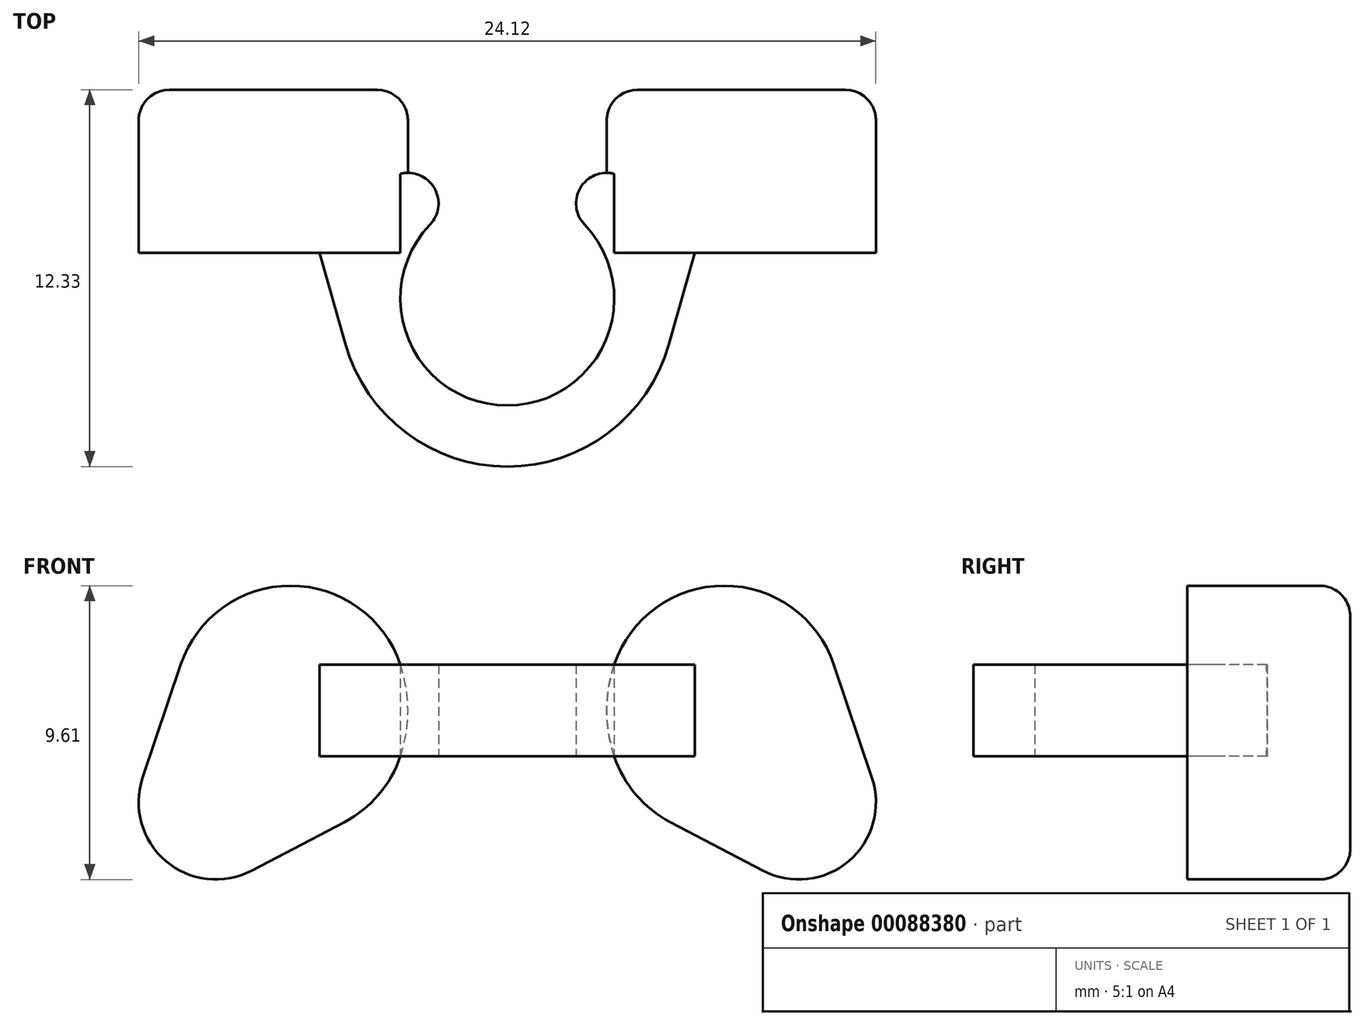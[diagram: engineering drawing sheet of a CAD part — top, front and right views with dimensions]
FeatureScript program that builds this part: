
annotation { "Feature Type Name" : "Feature", "Feature Type Description" : "" }
export const myFeature = defineFeature(function(context is Context, id is Id, definition is map)
    precondition{}
    {
        {
            var Q0;
            Q0=qCreatedBy(makeId("Top.planeOp"),FACE);
            var sketch = newSketch(context, id + "F0", { "sketchPlane" : qUnion([Q0])});
            skLineSegment(sketch, "E0", {"start": v(-2.53, 0) * mm, "end": v(2.53, 0) * mm, "construction": true});
            skArc(sketch, "E1", {"start": v(-2.53, 0) * mm, "mid": v(0, -5.92) * mm, "end": v(2.53, 0) * mm});
            skLineSegment(sketch, "E2", {"start": v(0, -2.42) * mm, "end": v(2.53, 0) * mm, "construction": true});
            skLineSegment(sketch, "E3", {"start": v(2.53, 0) * mm, "end": v(3.97, 1.38) * mm, "construction": true});
            skLineSegment(sketch, "E4", {"start": v(0, -2.42) * mm, "end": v(-2.53, 0) * mm, "construction": true});
            skLineSegment(sketch, "E5", {"start": v(-2.53, 0) * mm, "end": v(-3.97, 1.38) * mm, "construction": true});
            skArc(sketch, "E6", {"start": v(-2.53, 0) * mm, "mid": v(-2.56, 1.41) * mm, "end": v(-3.97, 1.38) * mm});
            skArc(sketch, "E7", {"start": v(3.97, 1.38) * mm, "mid": v(2.56, 1.41) * mm, "end": v(2.53, 0) * mm});
            skArc(sketch, "E8", {"start": v(-3.97, 1.38) * mm, "mid": v(0, -7.92) * mm, "end": v(3.97, 1.38) * mm});
            skArc(sketch, "E9", {"start": v(3.97, 1.38) * mm, "mid": v(0, 3.08) * mm, "end": v(-3.97, 1.38) * mm, "construction": true});
            skLineSegment(sketch, "E10", {"start": v(0, -2.42) * mm, "end": v(11, -2.42) * mm, "construction": true});
            skLineSegment(sketch, "E11", {"start": v(0, -2.42) * mm, "end": v(-11, -2.42) * mm, "construction": true});
            skLineSegment(sketch, "E12.bottom", {"start": v(-11, -2.42) * mm, "end": v(-5.5, -2.42) * mm});
            skLineSegment(sketch, "E12.top", {"start": v(-11, -7.92) * mm, "end": v(-5.5, -7.92) * mm});
            skLineSegment(sketch, "E12.left", {"start": v(-11, -2.42) * mm, "end": v(-11, -7.92) * mm});
            skLineSegment(sketch, "E12.right", {"start": v(-5.5, -2.42) * mm, "end": v(-5.5, -7.92) * mm});
            skLineSegment(sketch, "E13.bottom", {"start": v(11, -2.42) * mm, "end": v(5.5, -2.42) * mm});
            skLineSegment(sketch, "E13.top", {"start": v(11, -7.92) * mm, "end": v(5.5, -7.92) * mm});
            skLineSegment(sketch, "E13.left", {"start": v(11, -2.42) * mm, "end": v(11, -7.92) * mm});
            skLineSegment(sketch, "E13.right", {"start": v(5.5, -2.42) * mm, "end": v(5.5, -7.92) * mm});
            skLineSegment(sketch, "E14", {"start": v(-10.9, -2.42) * mm, "end": v(-10.9, -7.92) * mm});
            skLineSegment(sketch, "E15", {"start": v(10.9, -2.42) * mm, "end": v(10.9, -7.92) * mm});
            skSolve(sketch);
        }
        {
            var Q0;
            {var subQ0=sQuery(id+"F0.wireOp",EDGE,"E12.right");Q0=makeQuery(id+"F0.imprint","IMPRINT",FACE,{"disambiguationData":[TD([[makeQuery(id+"F0.imprint","IMPRINT",EDGE,{"derivedFrom":subQ0}),-1.0]])]});}
            var Q1;
            Q1=sQuery(id+"F0.wireOp",EDGE,"E12.right");
            revolve(context, id + "F1", {"entities" : qUnion([Q0]), "axis" : qUnion([Q1]), "revolveType" : RevolveType.FULL});
        }
        {
            var Q0;
            Q0=makeQuery(id+"F0.imprint","IMPRINT",FACE,{"disambiguationData":[TD([[makeQuery(id+"F0.imprint","IMPRINT",EDGE,{"derivedFrom":sQuery(id+"F0.wireOp",EDGE,"E1")}),-1.0]])]});
            extrude(context, id + "F2", {"entities" : qUnion([Q0]), "operationType" : NewBodyOperationType.ADD, "endBound" : BoundingType.SYMMETRIC, "depth" : 3 * mm});
        }
        {
            var Q0;
            {var subQ0=sQuery(id+"F0.wireOp",EDGE,"E13.right");Q0=makeQuery(id+"F0.imprint","IMPRINT",FACE,{"disambiguationData":[TD([[makeQuery(id+"F0.imprint","IMPRINT",EDGE,{"derivedFrom":subQ0}),1.0]])]});}
            var Q1;
            Q1=sQuery(id+"F0.wireOp",EDGE,"E13.right");
            revolve(context, id + "F3", {"operationType" : NewBodyOperationType.ADD, "entities" : qUnion([Q0]), "axis" : qUnion([Q1]), "revolveType" : RevolveType.FULL});
        }
        {
            var Q0;
            Q0=qCreatedBy(makeId("Top.planeOp"),FACE);
            var sketch = newSketch(context, id + "F4", { "sketchPlane" : qUnion([Q0])});
            skArc(sketch, "E16.0", {"start": v(-2.53, 0) * mm, "mid": v(0, -5.92) * mm, "end": v(2.53, 0) * mm});
            skLineSegment(sketch, "E17", {"start": v(-2.53, 0) * mm, "end": v(2.53, 0) * mm});
            skSolve(sketch);
        }
        {
            var Q0;
            Q0 = qSketchRegion(id + "F4", true);
            extrude(context, id + "F5", {"entities" : qUnion([Q0]), "operationType" : NewBodyOperationType.REMOVE, "endBound" : BoundingType.SYMMETRIC, "oppositeDirection" : true, "depth" : 25 * mm});
        }
        {
            var Q0;
            Q0=makeQuery(id+"F1.opRevolve","SWEPT_FACE",FACE,{"disambiguationData":[OSD([sQuery(id+"F0.wireOp",EDGE,"E12.bottom")])]});
            var sketch = newSketch(context, id + "F6", { "sketchPlane" : qUnion([Q0])});
            skLineSegment(sketch, "E18.0", {"start": v(3.5, 5.02) * mm, "end": v(3.5, 1.5) * mm});
            skLineSegment(sketch, "E19.0", {"start": v(-3.5, 1.5) * mm, "end": v(-3.5, 5.02) * mm});
            skLineSegment(sketch, "E20", {"start": v(-3.5, 1.5) * mm, "end": v(3.5, 1.5) * mm});
            skLineSegment(sketch, "E21", {"start": v(3.5, 5.02) * mm, "end": v(-3.5, 5.02) * mm});
            skLineSegment(sketch, "E22.0", {"start": v(-3.5, -5.02) * mm, "end": v(-3.5, -1.5) * mm});
            skLineSegment(sketch, "E23.0", {"start": v(3.5, -1.5) * mm, "end": v(3.5, -5.02) * mm});
            skLineSegment(sketch, "E24", {"start": v(3.5, -1.5) * mm, "end": v(-3.5, -1.5) * mm});
            skLineSegment(sketch, "E25", {"start": v(-3.5, -5.02) * mm, "end": v(3.5, -5.02) * mm});
            skSolve(sketch);
        }
        {
            var Q0;
            Q0 = qSketchRegion(id + "F6", true);
            extrude(context, id + "F7", {"entities" : qUnion([Q0]), "operationType" : NewBodyOperationType.REMOVE, "oppositeDirection" : true, "depth" : 25 * mm});
        }
        {
            var Q0;
            Q0=makeQuery(id+"F3.opRevolve","SWEPT_FACE",FACE,{"disambiguationData":[OSD([sQuery(id+"F0.wireOp",EDGE,"E13.top")])]});
            var sketch = newSketch(context, id + "F8", { "sketchPlane" : qUnion([Q0])});
            skArc(sketch, "E26", {"start": v(3.5, -1.5) * mm, "mid": v(7.1, -4.08) * mm, "end": v(10.69, -1.5) * mm});
            skArc(sketch, "E27", {"start": v(10.69, 1.5) * mm, "mid": v(7.1, 4.08) * mm, "end": v(3.5, 1.5) * mm});
            skSolve(sketch);
        }
        {
            var Q0;
            Q0 = qSketchRegion(id + "F8", true);
            var Q1;
            {var subQ0=sQuery(id+"F8.wireOp",EDGE,"E26");Q1=makeQuery(id+"F8.imprint","IMPRINT",FACE,{"disambiguationData":[TD([[makeQuery(id+"F8.imprint","IMPRINT",EDGE,{"derivedFrom":subQ0}),-1.0]])]});}
            var Q2;
            {var subQ0=sQuery(id+"F8.wireOp",EDGE,"E27");Q2=makeQuery(id+"F8.imprint","IMPRINT",FACE,{"disambiguationData":[TD([[makeQuery(id+"F8.imprint","IMPRINT",EDGE,{"derivedFrom":subQ0}),-1.0]])]});}
            extrude(context, id + "F9", {"entities" : qUnion([Q0, Q1, Q2]), "operationType" : NewBodyOperationType.REMOVE, "oppositeDirection" : true, "depth" : 25 * mm});
        }
        {
            var Q0;
            Q0=makeQuery(id+"F3.opRevolve","SWEPT_FACE",FACE,{"disambiguationData":[OSD([sQuery(id+"F0.wireOp",EDGE,"E13.top")])]});
            var sketch = newSketch(context, id + "F10", { "sketchPlane" : qUnion([Q0])});
            skLineSegment(sketch, "E28.0", {"start": v(-0.31, -1.5) * mm, "end": v(0.31, -1.5) * mm});
            skLineSegment(sketch, "E29.0", {"start": v(-0.31, 1.5) * mm, "end": v(0.31, 1.5) * mm});
            skLineSegment(sketch, "E30", {"start": v(0, -1.5) * mm, "end": v(0, 1.5) * mm});
            skLineSegment(sketch, "E31", {"start": v(-0.31, -1.5) * mm, "end": v(-0.31, 1.5) * mm});
            skSolve(sketch);
        }
        {
            var Q0;
            {var subQ2=sQuery(id+"F10.wireOp",EDGE,"E30");Q0=makeQuery(id+"F10.imprint","IMPRINT",FACE,{"disambiguationData":[TD([[makeQuery(id+"F10.imprint","IMPRINT",EDGE,{"derivedFrom":subQ2}),1.0]])]});}
            var Q1;
            Q1=makeQuery(id+"F1.opRevolve","SWEPT_FACE",FACE,{"disambiguationData":[OSD([sQuery(id+"F0.wireOp",EDGE,"E12.top")])]});
            extrude(context, id + "F11", {"entities" : qUnion([Q0, Q1]), "operationType" : NewBodyOperationType.REMOVE, "oppositeDirection" : true, "depth" : 25 * mm});
        }
        {
            var Q0;
            Q0=makeQuery(id+"F3.opRevolve","SWEPT_FACE",FACE,{"disambiguationData":[OSD([sQuery(id+"F0.wireOp",EDGE,"E13.top")])]});
            var sketch = newSketch(context, id + "F12", { "sketchPlane" : qUnion([Q0])});
            skArc(sketch, "E32.0.0", {"start": v(10.69, -1.5) * mm, "mid": v(10.9, 0) * mm, "end": v(10.69, 1.5) * mm});
            skArc(sketch, "E32.0.1", {"start": v(10.69, 1.5) * mm, "mid": v(7.1, 4.08) * mm, "end": v(3.5, 1.5) * mm});
            skLineSegment(sketch, "E32.0.2", {"start": v(3.5, 1.5) * mm, "end": v(0.31, 1.5) * mm});
            skArc(sketch, "E32.0.3", {"start": v(0.31, 1.5) * mm, "mid": v(0.1, 0) * mm, "end": v(0.31, -1.5) * mm});
            skLineSegment(sketch, "E32.0.4", {"start": v(0.31, -1.5) * mm, "end": v(3.5, -1.5) * mm});
            skArc(sketch, "E32.0.5", {"start": v(3.5, -1.5) * mm, "mid": v(7.1, -4.08) * mm, "end": v(10.69, -1.5) * mm});
            skArc(sketch, "E33", {"start": v(3.5, 1.5) * mm, "mid": v(3.25, 0) * mm, "end": v(3.5, -1.5) * mm});
            skSolve(sketch);
        }
        {
            var Q0;
            Q0=makeQuery(id+"F12.imprint","IMPRINT",FACE,{"disambiguationData":[TD([[makeQuery(id+"F12.imprint","IMPRINT",EDGE,{"derivedFrom":sQuery(id+"F12.wireOp",EDGE,"E32.0.0")}),-1.0]])]});
            extrude(context, id + "F13", {"entities" : qUnion([Q0]), "operationType" : NewBodyOperationType.ADD, "oppositeDirection" : true, "depth" : 9.33 * mm});
        }
        {
            var Q0;
            {var subQ0=sQuery(id+"F0.wireOp",EDGE,"E1");var subQ2=sQuery(id+"F0.wireOp",EDGE,"E7");var subQ3=makeQuery(id+"F2.opExtrude","SWEPT_FACE",FACE,{"disambiguationData":[OSD([subQ2])]});var subQ4=sQuery(id+"F0.wireOp",EDGE,"E8");Q0=makeQuery(id+"F3.boolean.opBoolean","SPLIT",FACE,{"disambiguationData":[TD([subQ3])],"derivedFrom":makeQuery(id+"F2.boolean.opBoolean","SPLIT",FACE,{"disambiguationData":[TD([makeQuery(id+"F1.opRevolve","SWEPT_FACE",FACE,{"disambiguationData":[OSD([sQuery(id+"F0.wireOp",EDGE,"E14")])]})])],"derivedFrom":makeQuery(id+"F2.opExtrude","CAP_FACE",FACE,{"disambiguationData":[OSD([subQ0,sQuery(id+"F0.wireOp",EDGE,"E6"),subQ2,subQ4])],"isStart":false})})});}
            var sketch = newSketch(context, id + "F14", { "sketchPlane" : qUnion([Q0])});
            skArc(sketch, "E34.0", {"start": v(0, -5.92) * mm, "mid": v(2.47, -4.9) * mm, "end": v(3.5, -2.42) * mm});
            skArc(sketch, "E35.0", {"start": v(3.5, -2.42) * mm, "mid": v(3.25, -1.12) * mm, "end": v(2.53, 0) * mm});
            skLineSegment(sketch, "E36", {"start": v(2.53, 0) * mm, "end": v(0, -5.92) * mm});
            skArc(sketch, "E37.0", {"start": v(3.95, 1.4) * mm, "mid": v(2.55, 1.4) * mm, "end": v(2.53, 0) * mm});
            skLineSegment(sketch, "E38", {"start": v(3.95, 1.4) * mm, "end": v(3.95, 2.22) * mm});
            skLineSegment(sketch, "E39", {"start": v(3.95, 2.22) * mm, "end": v(1.16, 2.22) * mm});
            skLineSegment(sketch, "E40", {"start": v(1.16, 2.22) * mm, "end": v(1.26, -2.96) * mm});
            skSolve(sketch);
        }
        {
            var Q0;
            {var subQ0=sQuery(id+"F14.wireOp",EDGE,"E34.0");Q0=makeQuery(id+"F14.imprint","IMPRINT",FACE,{"disambiguationData":[TD([[makeQuery(id+"F14.imprint","IMPRINT",EDGE,{"derivedFrom":subQ0}),1.0]])]});}
            var Q1;
            {var subQ0=sQuery(id+"F14.wireOp",EDGE,"E37.0");Q1=makeQuery(id+"F14.imprint","IMPRINT",FACE,{"disambiguationData":[TD([[makeQuery(id+"F14.imprint","IMPRINT",EDGE,{"derivedFrom":subQ0}),-1.0]])]});}
            extrude(context, id + "F15", {"entities" : qUnion([Q0, Q1]), "operationType" : NewBodyOperationType.REMOVE, "oppositeDirection" : true, "depth" : 25 * mm});
        }
        {
            var Q0;
            Q0=makeQuery(id+"F3.opRevolve","SWEPT_FACE",FACE,{"disambiguationData":[OSD([sQuery(id+"F0.wireOp",EDGE,"E13.top")])]});
            var sketch = newSketch(context, id + "F16", { "sketchPlane" : qUnion([Q0])});
            skArc(sketch, "E41.0.0", {"start": v(10.69, 1.5) * mm, "mid": v(7.1, 4.08) * mm, "end": v(3.5, 1.5) * mm});
            skLineSegment(sketch, "E41.0.1", {"start": v(3.5, 1.5) * mm, "end": v(0.31, 1.5) * mm});
            skArc(sketch, "E41.0.2", {"start": v(0.31, 1.5) * mm, "mid": v(0.1, 0) * mm, "end": v(0.31, -1.5) * mm});
            skLineSegment(sketch, "E41.0.3", {"start": v(0.31, -1.5) * mm, "end": v(3.5, -1.5) * mm});
            skArc(sketch, "E41.0.4", {"start": v(3.5, -1.5) * mm, "mid": v(7.1, -4.08) * mm, "end": v(10.69, -1.5) * mm});
            skArc(sketch, "E41.0.5", {"start": v(10.69, -1.5) * mm, "mid": v(10.9, 0) * mm, "end": v(10.69, 1.5) * mm});
            skLineSegment(sketch, "E42.0", {"start": v(-5.5, 0) * mm, "end": v(5.5, 0) * mm});
            skLineSegment(sketch, "E43", {"start": v(3.5, 1.5) * mm, "end": v(5.5, 1.5) * mm});
            skLineSegment(sketch, "E44", {"start": v(3.5, -1.5) * mm, "end": v(5.5, -1.5) * mm});
            skLineSegment(sketch, "E45", {"start": v(5.5, -1.5) * mm, "end": v(5.5, 1.5) * mm});
            skSolve(sketch);
        }
        {
            var Q0;
            Q0=makeQuery(id+"F16.imprint","IMPRINT",FACE,{"disambiguationData":[TD([[makeQuery(id+"F16.imprint","IMPRINT",EDGE,{"derivedFrom":sQuery(id+"F16.wireOp",EDGE,"E41.0.0")}),1.0]])]});
            extrude(context, id + "F17", {"entities" : qUnion([Q0]), "operationType" : NewBodyOperationType.REMOVE, "oppositeDirection" : true, "depth" : 4 * mm});
        }
        {
            var Q0;
            {var subQ0=makeQuery(id+"F1.opRevolve","SWEPT_FACE",FACE,{"disambiguationData":[OSD([sQuery(id+"F0.wireOp",EDGE,"E14")])]});var subQ1=sQuery(id+"F0.wireOp",EDGE,"E1");var subQ3=sQuery(id+"F0.wireOp",EDGE,"E8");var subQ5=sQuery(id+"F0.wireOp",EDGE,"E7");Q0=makeQuery(id+"F17.boolean.opBoolean","MERGE",FACE,{"derivedFrom":[makeQuery(id+"F7.boolean.opBoolean","MERGE",FACE,{"derivedFrom":[makeQuery(id+"F3.boolean.opBoolean","SPLIT",FACE,{"disambiguationData":[TD([subQ0])],"derivedFrom":makeQuery(id+"F2.boolean.opBoolean","SPLIT",FACE,{"disambiguationData":[TD([subQ0])],"derivedFrom":makeQuery(id+"F2.opExtrude","CAP_FACE",FACE,{"disambiguationData":[OSD([subQ1,sQuery(id+"F0.wireOp",EDGE,"E6"),subQ5,subQ3])],"isStart":false})})}),makeQuery(id+"F7.opExtrude","SWEPT_FACE",FACE,{"disambiguationData":[OSD([sQuery(id+"F6.wireOp",EDGE,"E20")])]})]}),makeQuery(id+"F17.opExtrude","SWEPT_FACE",FACE,{"disambiguationData":[OSD([sQuery(id+"F16.wireOp",EDGE,"E43")])]})]});}
            var sketch = newSketch(context, id + "F18", { "sketchPlane" : qUnion([Q0])});
            skArc(sketch, "E46.0", {"start": v(-3.97, 1.38) * mm, "mid": v(0, -7.92) * mm, "end": v(3.97, 1.38) * mm});
            skLineSegment(sketch, "E47.0", {"start": v(5.5, -3.92) * mm, "end": v(5.5, -7.92) * mm});
            skLineSegment(sketch, "E48.0", {"start": v(0.31, -7.92) * mm, "end": v(5.5, -7.92) * mm});
            skSolve(sketch);
        }
        {
            var Q0;
            {var subQ0=sQuery(id+"F18.wireOp",EDGE,"E47.0");Q0=makeQuery(id+"F18.imprint","IMPRINT",FACE,{"disambiguationData":[TD([[makeQuery(id+"F18.imprint","IMPRINT",EDGE,{"derivedFrom":subQ0}),-1.0]])]});}
            extrude(context, id + "F19", {"entities" : qUnion([Q0]), "operationType" : NewBodyOperationType.REMOVE, "oppositeDirection" : true, "depth" : 25 * mm});
        }
        {
            var Q0;
            {var subQ0=sQuery(id+"F16.wireOp",EDGE,"E43");Q0=makeQuery(id+"F19.boolean.opBoolean","MERGE",FACE,{"derivedFrom":[makeQuery(id+"F17.boolean.opBoolean","COPY",FACE,{"derivedFrom":makeQuery(id+"F17.opExtrude","CAP_FACE",FACE,{"disambiguationData":[OSD([sQuery(id+"F16.wireOp",EDGE,"E41.0.0"),sQuery(id+"F16.wireOp",EDGE,"E41.0.4"),sQuery(id+"F16.wireOp",EDGE,"E41.0.5"),subQ0,sQuery(id+"F16.wireOp",EDGE,"E44"),sQuery(id+"F16.wireOp",EDGE,"E45")])],"isStart":false})}),makeQuery(id+"F19.opExtrude","SWEPT_FACE",FACE,{"disambiguationData":[OSD([subQ0])]})]});}
            extrude(context, id + "F20", {"entities" : qUnion([Q0]), "operationType" : NewBodyOperationType.REMOVE, "oppositeDirection" : true, "depth" : 3 * mm});
        }
        {
            var Q0;
            Q0=makeQuery(id+"F13.opExtrude","CAP_FACE",FACE,{"disambiguationData":[OSD([sQuery(id+"F12.wireOp",EDGE,"E32.0.0"),sQuery(id+"F12.wireOp",EDGE,"E32.0.1"),sQuery(id+"F12.wireOp",EDGE,"E32.0.5"),sQuery(id+"F12.wireOp",EDGE,"E33")])],"isStart":false});
            extrude(context, id + "F21", {"entities" : qUnion([Q0]), "operationType" : NewBodyOperationType.ADD, "depth" : 3 * mm});
        }
        {
            var Q0;
            Q0=makeQuery(id+"F21.opExtrude","CAP_FACE",FACE,{"disambiguationData":[OSD([sQuery(id+"F12.wireOp",EDGE,"E32.0.0"),sQuery(id+"F12.wireOp",EDGE,"E32.0.1"),sQuery(id+"F12.wireOp",EDGE,"E32.0.5"),sQuery(id+"F12.wireOp",EDGE,"E33")])],"isStart":false});
            var sketch = newSketch(context, id + "F22", { "sketchPlane" : qUnion([Q0])});
            skArc(sketch, "E49.0", {"start": v(-10.69, 1.5) * mm, "mid": v(-7.1, 4.08) * mm, "end": v(-3.5, 1.5) * mm});
            skArc(sketch, "E50.0", {"start": v(-3.5, -1.5) * mm, "mid": v(-7.1, -4.08) * mm, "end": v(-10.69, -1.5) * mm});
            skArc(sketch, "E51", {"start": v(-3.5, -1.5) * mm, "mid": v(-3.25, 0) * mm, "end": v(-3.5, 1.5) * mm});
            skLineSegment(sketch, "E52.0", {"start": v(-3.95, -1.5) * mm, "end": v(-3.95, 1.5) * mm});
            skLineSegment(sketch, "E53.0", {"start": v(-3.5, 1.5) * mm, "end": v(-3.95, 1.5) * mm});
            skLineSegment(sketch, "E54.0", {"start": v(-3.5, -1.5) * mm, "end": v(-3.95, -1.5) * mm});
            skSolve(sketch);
        }
        {
            var Q0;
            Q0 = qSketchRegion(id + "F22", true);
            extrude(context, id + "F23", {"entities" : qUnion([Q0]), "operationType" : NewBodyOperationType.ADD, "endBound" : BoundingType.UP_TO_NEXT, "oppositeDirection" : true, "depth" : 25 * mm});
        }
        {
            var Q0;
            Q0=makeQuery(id+"F23.boolean.opBoolean","MERGE",FACE,{"derivedFrom":[makeQuery(id+"F21.opExtrude","CAP_FACE",FACE,{"disambiguationData":[OSD([sQuery(id+"F12.wireOp",EDGE,"E32.0.0"),sQuery(id+"F12.wireOp",EDGE,"E32.0.1"),sQuery(id+"F12.wireOp",EDGE,"E32.0.5"),sQuery(id+"F12.wireOp",EDGE,"E33")])],"isStart":false}),makeQuery(id+"F23.opExtrude","CAP_FACE",FACE,{"disambiguationData":[OSD([sQuery(id+"F22.wireOp",EDGE,"E51"),sQuery(id+"F22.wireOp",EDGE,"E52.0"),sQuery(id+"F22.wireOp",EDGE,"E53.0"),sQuery(id+"F22.wireOp",EDGE,"E54.0")])],"isStart":true})]});
            var sketch = newSketch(context, id + "F24", { "sketchPlane" : qUnion([Q0])});
            skLineSegment(sketch, "E55", {"start": v(-10.69, 1.5) * mm, "end": v(-13.18, -5.9) * mm});
            skLineSegment(sketch, "E56", {"start": v(-13.18, -5.9) * mm, "end": v(-11.4, -6.83) * mm});
            skLineSegment(sketch, "E57", {"start": v(-11.4, -6.83) * mm, "end": v(-5.33, -3.65) * mm});
            skArc(sketch, "E58", {"start": v(-11.93, -2.2) * mm, "mid": v(-11.18, -4.92) * mm, "end": v(-8.37, -5.24) * mm});
            skArc(sketch, "E59.0", {"start": v(-3.5, -1.5) * mm, "mid": v(-7.1, -4.08) * mm, "end": v(-10.69, -1.5) * mm});
            skArc(sketch, "E60.0", {"start": v(-10.69, 1.5) * mm, "mid": v(-10.9, 0) * mm, "end": v(-10.69, -1.5) * mm});
            skSolve(sketch);
        }
        {
            var Q0;
            {var subQ4=sQuery(id+"F24.wireOp",EDGE,"E58");Q0=makeQuery(id+"F24.imprint","IMPRINT",FACE,{"disambiguationData":[TD([[makeQuery(id+"F24.imprint","IMPRINT",EDGE,{"derivedFrom":subQ4}),1.0]])]});}
            var Q1;
            Q1=makeQuery(id+"F20.boolean.opBoolean","COPY",FACE,{"derivedFrom":makeQuery(id+"F20.opExtrude","CAP_FACE",FACE,{"disambiguationData":[OSD([sQuery(id+"F16.wireOp",EDGE,"E41.0.0"),sQuery(id+"F16.wireOp",EDGE,"E41.0.4"),sQuery(id+"F16.wireOp",EDGE,"E41.0.5"),sQuery(id+"F16.wireOp",EDGE,"E43"),sQuery(id+"F16.wireOp",EDGE,"E44"),sQuery(id+"F16.wireOp",EDGE,"E45")])],"isStart":false})});
            extrude(context, id + "F25", {"entities" : qUnion([Q0]), "operationType" : NewBodyOperationType.ADD, "endBound" : BoundingType.UP_TO_SURFACE, "oppositeDirection" : true, "endBoundEntityFace" : qUnion([Q1]), "depth" : 25 * mm});
        }
        {
            var Q0;
            {var subQ0=sQuery(id+"F16.wireOp",EDGE,"E43");var subQ1=makeQuery(id+"F1.opRevolve","SWEPT_FACE",FACE,{"disambiguationData":[OSD([sQuery(id+"F0.wireOp",EDGE,"E14")])]});var subQ2=sQuery(id+"F0.wireOp",EDGE,"E1");var subQ4=sQuery(id+"F0.wireOp",EDGE,"E8");var subQ6=sQuery(id+"F0.wireOp",EDGE,"E7");var subQ7=makeQuery(id+"F2.opExtrude","SWEPT_FACE",FACE,{"disambiguationData":[OSD([subQ6])]});var subQ8=makeQuery(id+"F2.boolean.opBoolean","SPLIT",FACE,{"disambiguationData":[TD([subQ1])],"derivedFrom":makeQuery(id+"F2.opExtrude","CAP_FACE",FACE,{"disambiguationData":[OSD([subQ2,sQuery(id+"F0.wireOp",EDGE,"E6"),subQ6,subQ4])],"isStart":false})});Q0=makeQuery(id+"F20.boolean.opBoolean","MERGE",FACE,{"derivedFrom":[makeQuery(id+"F3.boolean.opBoolean","SPLIT",FACE,{"disambiguationData":[TD([subQ7])],"derivedFrom":subQ8}),makeQuery(id+"F17.boolean.opBoolean","MERGE",FACE,{"derivedFrom":[makeQuery(id+"F7.boolean.opBoolean","MERGE",FACE,{"derivedFrom":[makeQuery(id+"F3.boolean.opBoolean","SPLIT",FACE,{"disambiguationData":[TD([subQ1])],"derivedFrom":subQ8}),makeQuery(id+"F7.opExtrude","SWEPT_FACE",FACE,{"disambiguationData":[OSD([sQuery(id+"F6.wireOp",EDGE,"E20")])]})]}),makeQuery(id+"F17.opExtrude","SWEPT_FACE",FACE,{"disambiguationData":[OSD([subQ0])]})]}),makeQuery(id+"F20.opExtrude","SWEPT_FACE",FACE,{"disambiguationData":[OSD([subQ0])]})]});}
            var sketch = newSketch(context, id + "F26", { "sketchPlane" : qUnion([Q0])});
            skArc(sketch, "E61.0", {"start": v(0.31, -7.91) * mm, "mid": v(3.44, -6.71) * mm, "end": v(5.3, -3.92) * mm});
            skLineSegment(sketch, "E62", {"start": v(5.3, -3.92) * mm, "end": v(5.3, -0.92) * mm});
            skLineSegment(sketch, "E63", {"start": v(5.3, -0.92) * mm, "end": v(6.14, -0.92) * mm});
            skLineSegment(sketch, "E64", {"start": v(5.3, -3.92) * mm, "end": v(6.14, -0.92) * mm});
            skSolve(sketch);
        }
        {
            var Q0;
            Q0 = qSketchRegion(id + "F26", true);
            var Q1;
            {var subQ0=sQuery(id+"F16.wireOp",EDGE,"E44");var subQ1=makeQuery(id+"F1.opRevolve","SWEPT_FACE",FACE,{"disambiguationData":[OSD([sQuery(id+"F0.wireOp",EDGE,"E14")])]});var subQ2=sQuery(id+"F0.wireOp",EDGE,"E1");var subQ4=sQuery(id+"F0.wireOp",EDGE,"E8");var subQ6=sQuery(id+"F0.wireOp",EDGE,"E7");var subQ7=makeQuery(id+"F2.opExtrude","SWEPT_FACE",FACE,{"disambiguationData":[OSD([subQ6])]});var subQ8=makeQuery(id+"F2.boolean.opBoolean","SPLIT",FACE,{"disambiguationData":[TD([subQ1])],"derivedFrom":makeQuery(id+"F2.opExtrude","CAP_FACE",FACE,{"disambiguationData":[OSD([subQ2,sQuery(id+"F0.wireOp",EDGE,"E6"),subQ6,subQ4])],"isStart":true})});Q1=makeQuery(id+"F20.boolean.opBoolean","MERGE",FACE,{"derivedFrom":[makeQuery(id+"F3.boolean.opBoolean","SPLIT",FACE,{"disambiguationData":[TD([subQ7])],"derivedFrom":subQ8}),makeQuery(id+"F17.boolean.opBoolean","MERGE",FACE,{"derivedFrom":[makeQuery(id+"F7.boolean.opBoolean","MERGE",FACE,{"derivedFrom":[makeQuery(id+"F3.boolean.opBoolean","SPLIT",FACE,{"disambiguationData":[TD([subQ1])],"derivedFrom":subQ8}),makeQuery(id+"F7.opExtrude","SWEPT_FACE",FACE,{"disambiguationData":[OSD([sQuery(id+"F6.wireOp",EDGE,"E24")])]})]}),makeQuery(id+"F17.opExtrude","SWEPT_FACE",FACE,{"disambiguationData":[OSD([subQ0])]})]}),makeQuery(id+"F20.opExtrude","SWEPT_FACE",FACE,{"disambiguationData":[OSD([subQ0])]})]});}
            extrude(context, id + "F27", {"entities" : qUnion([Q0]), "operationType" : NewBodyOperationType.ADD, "endBound" : BoundingType.UP_TO_SURFACE, "oppositeDirection" : true, "endBoundEntityFace" : qUnion([Q1]), "depth" : 25 * mm});
        }
        {
            var Q0;
            {var subQ0=sQuery(id+"F16.wireOp",EDGE,"E43");var subQ1=makeQuery(id+"F1.opRevolve","SWEPT_FACE",FACE,{"disambiguationData":[OSD([sQuery(id+"F0.wireOp",EDGE,"E14")])]});var subQ2=sQuery(id+"F0.wireOp",EDGE,"E1");var subQ4=sQuery(id+"F0.wireOp",EDGE,"E8");var subQ6=sQuery(id+"F0.wireOp",EDGE,"E7");var subQ7=makeQuery(id+"F2.opExtrude","SWEPT_FACE",FACE,{"disambiguationData":[OSD([subQ6])]});var subQ8=makeQuery(id+"F2.boolean.opBoolean","SPLIT",FACE,{"disambiguationData":[TD([subQ1])],"derivedFrom":makeQuery(id+"F2.opExtrude","CAP_FACE",FACE,{"disambiguationData":[OSD([subQ2,sQuery(id+"F0.wireOp",EDGE,"E6"),subQ6,subQ4])],"isStart":false})});Q0=makeQuery(id+"F27.boolean.opBoolean","MERGE",FACE,{"derivedFrom":[makeQuery(id+"F20.boolean.opBoolean","MERGE",FACE,{"derivedFrom":[makeQuery(id+"F3.boolean.opBoolean","SPLIT",FACE,{"disambiguationData":[TD([subQ7])],"derivedFrom":subQ8}),makeQuery(id+"F17.boolean.opBoolean","MERGE",FACE,{"derivedFrom":[makeQuery(id+"F7.boolean.opBoolean","MERGE",FACE,{"derivedFrom":[makeQuery(id+"F3.boolean.opBoolean","SPLIT",FACE,{"disambiguationData":[TD([subQ1])],"derivedFrom":subQ8}),makeQuery(id+"F7.opExtrude","SWEPT_FACE",FACE,{"disambiguationData":[OSD([sQuery(id+"F6.wireOp",EDGE,"E20")])]})]}),makeQuery(id+"F17.opExtrude","SWEPT_FACE",FACE,{"disambiguationData":[OSD([subQ0])]})]}),makeQuery(id+"F20.opExtrude","SWEPT_FACE",FACE,{"disambiguationData":[OSD([subQ0])]})]}),makeQuery(id+"F27.opExtrude","CAP_FACE",FACE,{"disambiguationData":[OSD([sQuery(id+"F26.wireOp",EDGE,"E62"),sQuery(id+"F26.wireOp",EDGE,"E63"),sQuery(id+"F26.wireOp",EDGE,"E64")])],"isStart":true})]});}
            var sketch = newSketch(context, id + "F28", { "sketchPlane" : qUnion([Q0])});
            skArc(sketch, "E65.0", {"start": v(0.31, -7.91) * mm, "mid": v(3.44, -6.71) * mm, "end": v(5.3, -3.92) * mm});
            skArc(sketch, "E66.0", {"start": v(0, -7.92) * mm, "mid": v(0.16, -7.92) * mm, "end": v(0.31, -7.91) * mm});
            skLineSegment(sketch, "E67", {"start": v(0.5, -7.9) * mm, "end": v(0.5, -8.4) * mm});
            skLineSegment(sketch, "E68", {"start": v(0.5, -8.4) * mm, "end": v(0, -8.4) * mm});
            skLineSegment(sketch, "E69", {"start": v(0, -8.4) * mm, "end": v(0, -7.92) * mm});
            skSolve(sketch);
        }
        {
            var Q0;
            {var subQ1=sQuery(id+"F28.wireOp",EDGE,"E66.0");Q0=makeQuery(id+"F28.imprint","IMPRINT",FACE,{"disambiguationData":[TD([[makeQuery(id+"F28.imprint","IMPRINT",EDGE,{"derivedFrom":subQ1}),-1.0]])]});}
            extrude(context, id + "F29", {"entities" : qUnion([Q0]), "operationType" : NewBodyOperationType.REMOVE, "oppositeDirection" : true, "depth" : 25 * mm});
        }
        {
            var Q0;
            Q0=makeQuery(id+"F1.opRevolve","SWEPT_BODY",BODY,{"disambiguationData":[OSD([sQuery(id+"F0.wireOp",EDGE,"E12.bottom"),sQuery(id+"F0.wireOp",EDGE,"E12.top"),sQuery(id+"F0.wireOp",EDGE,"E12.right"),sQuery(id+"F0.wireOp",EDGE,"E14")])]});
            var Q1;
            Q1=makeQuery(id+"F11.boolean.opBoolean","COPY",FACE,{"derivedFrom":makeQuery(id+"F11.opExtrude","SWEPT_FACE",FACE,{"disambiguationData":[OSD([sQuery(id+"F10.wireOp",EDGE,"E30")])]})});
            mirror(context, id + "F30", {"operationType" : NewBodyOperationType.ADD, "entities" : qUnion([Q0]), "mirrorPlane" : qUnion([Q1])});
        }
        {
            var Q0;
            Q0=makeQuery(id+"F21.opExtrude","CAP_EDGE",EDGE,{"disambiguationData":[OSD([sQuery(id+"F12.wireOp",EDGE,"E32.0.1")])],"isStart":false});
            var Q1;
            Q1=makeQuery(id+"F30.opPattern","COPY",EDGE,{"derivedFrom":makeQuery(id+"F21.opExtrude","CAP_EDGE",EDGE,{"disambiguationData":[OSD([sQuery(id+"F12.wireOp",EDGE,"E32.0.1")])],"isStart":false}),"instanceName":"1"});
            fillet(context, id + "F31", {"entities" : qUnion([Q0, Q1]), "radius" : 1 * mm, "tangentPropagation" : true, "allowEdgeOverflow" : false});
        }
    });
